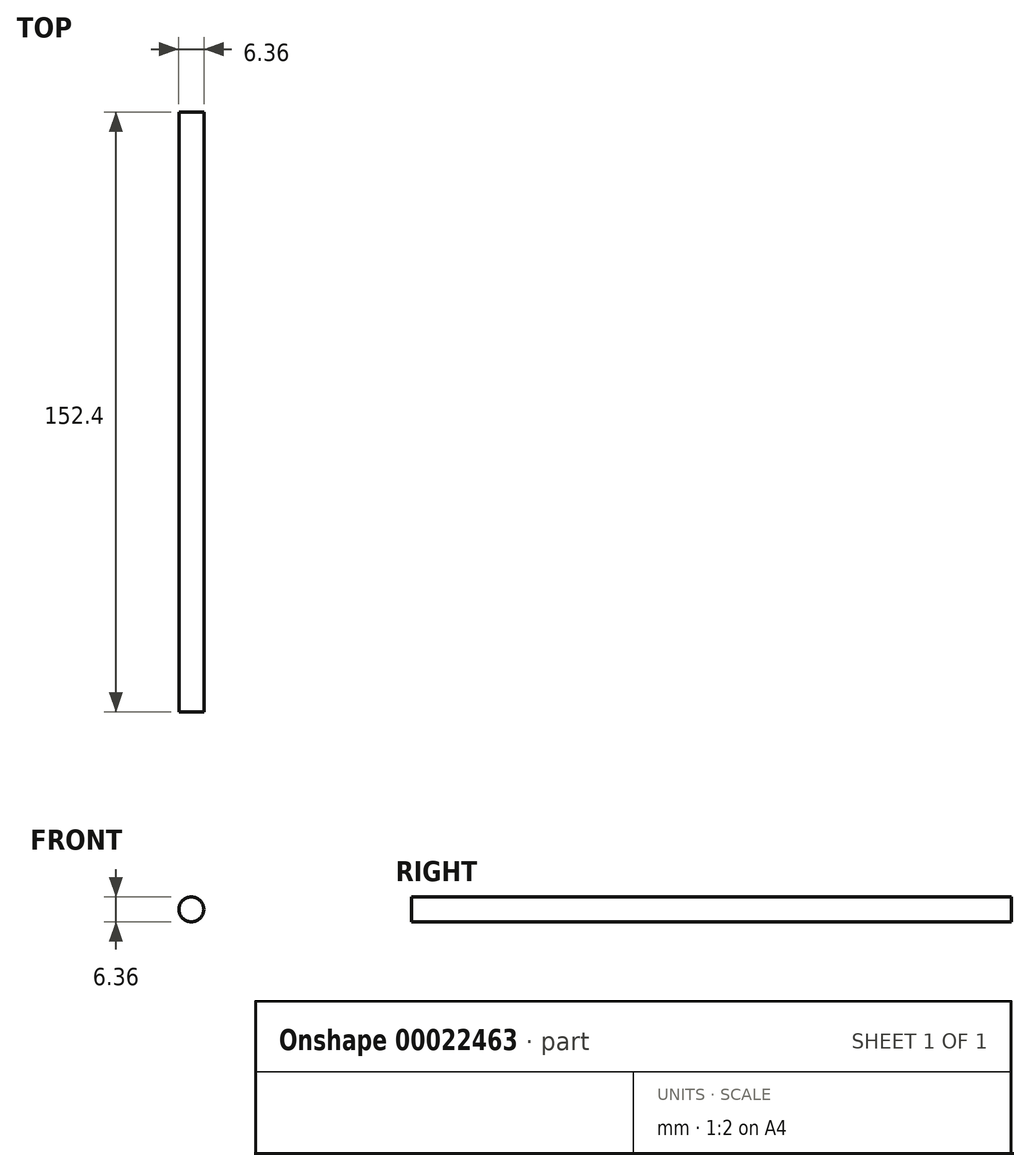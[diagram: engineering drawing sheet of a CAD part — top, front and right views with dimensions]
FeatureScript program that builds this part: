
annotation { "Feature Type Name" : "Feature", "Feature Type Description" : "" }
export const myFeature = defineFeature(function(context is Context, id is Id, definition is map)
    precondition{}
    {
        {
            var Q0;
            Q0=qCreatedBy(makeId("Front.planeOp"),FACE);
            var sketch = newSketch(context, id + "F0", { "sketchPlane" : qUnion([Q0])});
            skCircle(sketch, "E0", {"center": v(0, 0) * mm, "radius": 3.18 * mm});
            skSolve(sketch);
        }
        {
            var Q0;
            Q0 = qSketchRegion(id + "F0", true);
            extrude(context, id + "F1", {"entities" : qUnion([Q0]), "depth" : 152.4 * mm});
        }
    });
